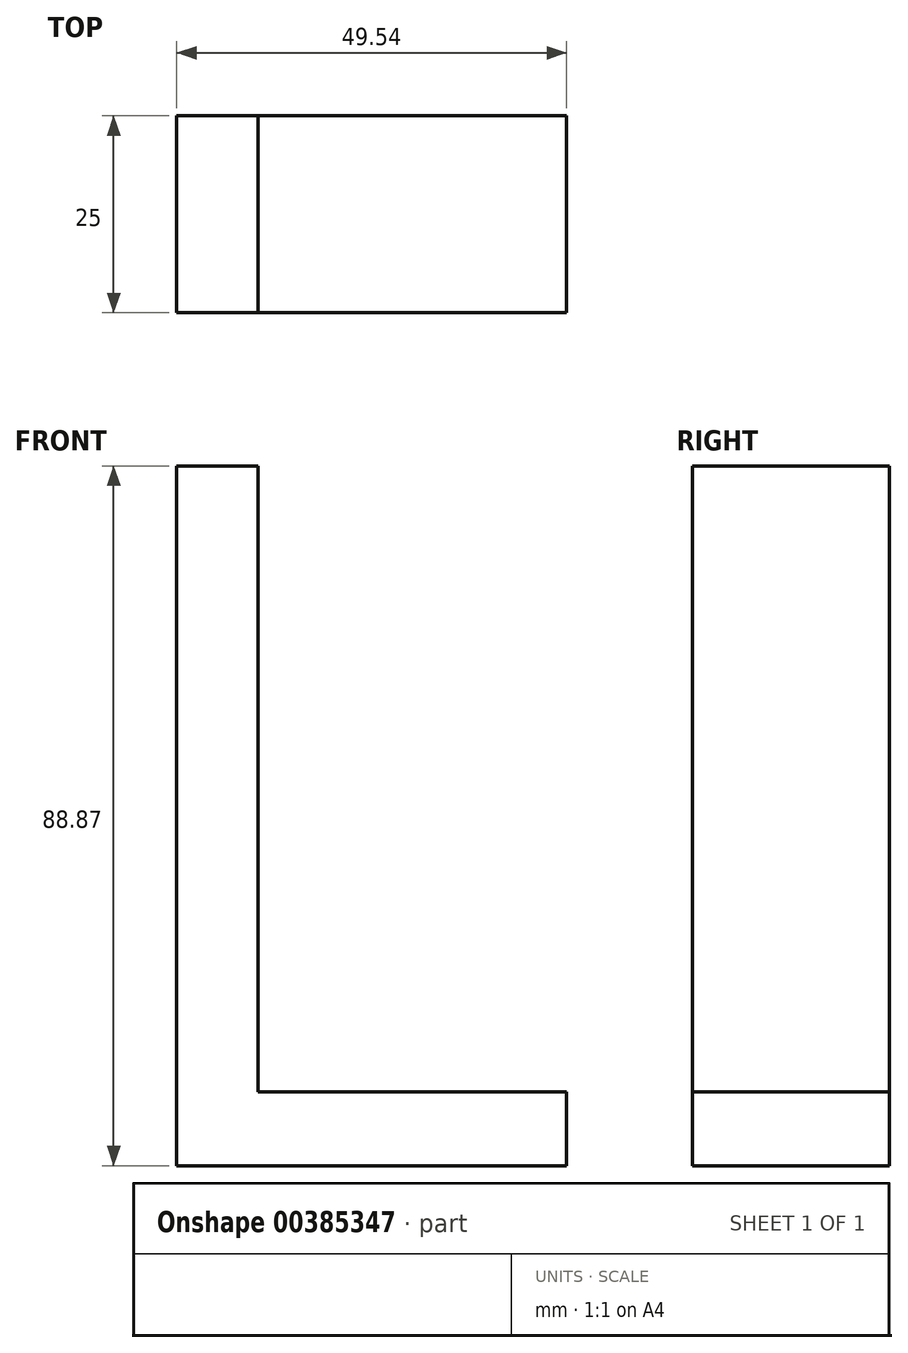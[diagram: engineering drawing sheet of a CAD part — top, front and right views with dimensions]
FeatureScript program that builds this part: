
annotation { "Feature Type Name" : "Feature", "Feature Type Description" : "" }
export const myFeature = defineFeature(function(context is Context, id is Id, definition is map)
    precondition{}
    {
        {
            var Q0;
            Q0=qCreatedBy(makeId("Front.planeOp"),FACE);
            var sketch = newSketch(context, id + "F0", { "sketchPlane" : qUnion([Q0])});
            skText(sketch, "E0", { "text": "L", "fontName": "OpenSans-Regular.ttf"});
            const initialGuessF0  = {"E0": [-0.05473, -0.04828, 1, 0, 0.08963]};
            skSetInitialGuess(sketch, initialGuessF0);
            skSolve(sketch);
        }
        {
            var Q0;
            Q0=qSketchRegion(id+"F0",true);
            extrude(context, id + "F1", {"entities" : qUnion([Q0]), "depth" : 25 * mm});
        }
    });
